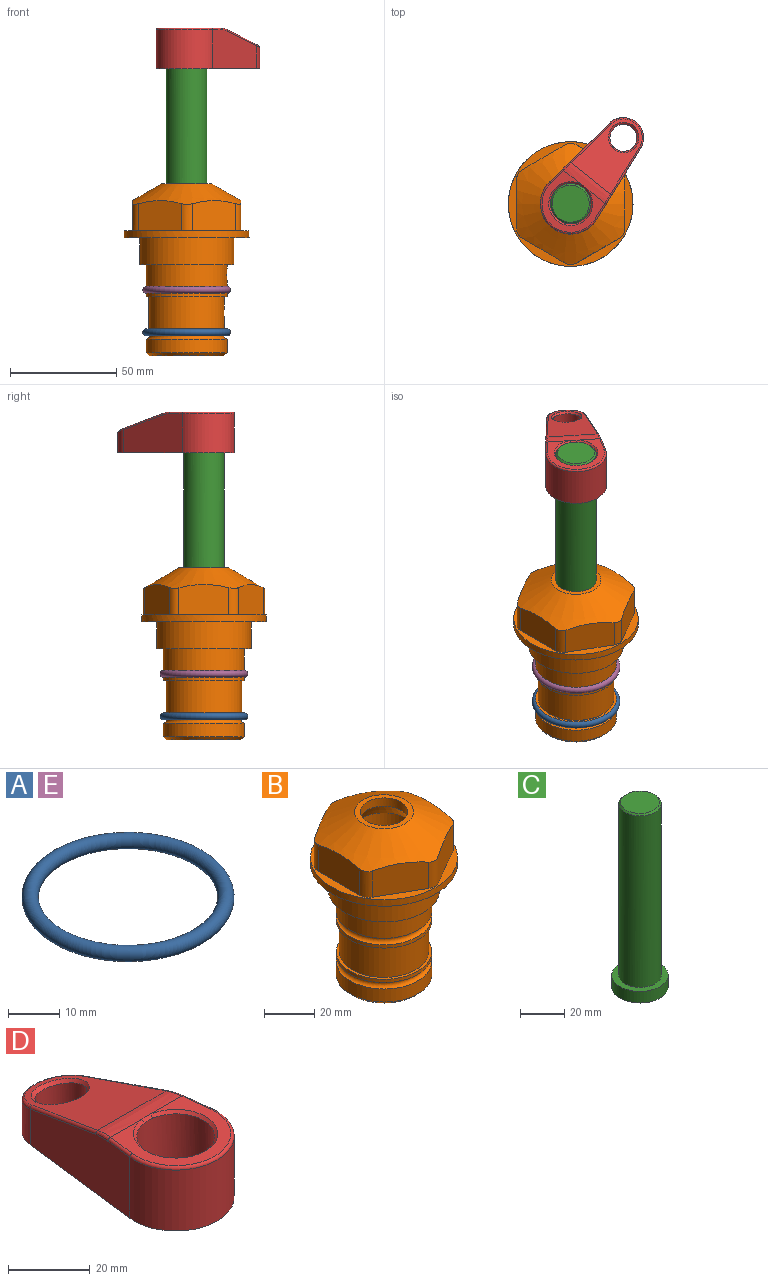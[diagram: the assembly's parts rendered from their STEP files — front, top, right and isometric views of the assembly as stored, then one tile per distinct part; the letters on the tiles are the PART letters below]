
ASSEMBLY  parts=5 mates=3
PART A: 1 faces, bbox 44.7x44.7x3.2 mm
  f0: torus R=19.05mm, axis (0,0,1), area 1193.9mm2
PART B: 36 faces, bbox 58.7x58.7x81 mm
  f0: cylinder r=17.78mm len=35.56mm, axis (0,0,1), area 1670.8mm2, adj f23,f24,f31
  f1: cylinder r=19.05mm len=38.1mm, axis (0,0,1), area 1191.9mm2, adj f26,f27,f30
  f2: plane 58.66x58.66mm, normal (0,0,-1), area 1150.6mm2, adj f3,f28
  f3: cylinder r=29.33mm len=58.66mm, axis (0,0,-1), area 585.1mm2, adj f2,f4
  f4: plane 58.66x58.66mm, normal (0,0,1), area 475.9mm2, adj f3,f5,f6,f7,f8,f9,f10,f11
  f5: plane 20.32x14.34mm, normal (-0.5,0.87,0), area 324.4mm2, adj f4,f15,f16,f17
  f6: plane 20.32x14.34mm, normal (0.5,0.87,0), area 324.4mm2, adj f4,f14,f15,f17
  f7: plane 23.48x14.34mm, normal (1,0,0), area 324.4mm2, adj f4,f13,f14,f17
  f8: plane 20.32x14.34mm, normal (0.5,-0.87,0), area 324.4mm2, adj f4,f12,f13,f17
  f9: plane 20.32x14.34mm, normal (-0.5,-0.87,0), area 324.4mm2, adj f4,f11,f12,f17
  f10: plane 23.48x14.34mm, normal (-1,0,0), area 324.4mm2, adj f4,f11,f16,f17
  f11: cylinder r=5.08mm len=12.85mm, axis (0,0,-1), area 67.2mm2, adj f4,f9,f10,f17
  f12: cylinder r=5.08mm len=12.85mm, axis (0,0,-1), area 67.2mm2, adj f4,f8,f9,f17
  f13: cylinder r=5.08mm len=12.85mm, axis (0,0,-1), area 67.2mm2, adj f4,f7,f8,f17
  f14: cylinder r=5.08mm len=12.85mm, axis (0,0,-1), area 67.2mm2, adj f4,f6,f7,f17
  f15: cylinder r=5.08mm len=12.85mm, axis (0,0,-1), area 67.2mm2, adj f4,f5,f6,f17
  f16: cylinder r=5.08mm len=12.85mm, axis (0,0,-1), area 67.2mm2, adj f4,f5,f10,f17
  f17: cone r=11.73mm half-angle=60deg, axis (0,0,-1), area 2071.8mm2, adj f5,f6,f7,f8,f9,f10,f11,f12
  f18: plane 23.46x23.46mm, normal (0,0,1), area 147.4mm2, adj f17,f35
  f19: plane 34.93x34.93mm, normal (0,0,-1), area 958mm2, adj f29
  f20: cylinder r=19.05mm len=38.1mm, axis (0,0,1), area 760.1mm2, adj f21,f29
  f21: torus R=19.05mm, axis (0,0,1), area 565.3mm2, adj f20,f22
  f22: cylinder r=19.05mm len=38.1mm, axis (0,0,1), area 190mm2, adj f21,f23
  f23: plane 38.1x38.1mm, normal (0,0,1), area 146.9mm2, adj f0,f22
  f24: plane 38.1x38.1mm, normal (0,0,-1), area 146.9mm2, adj f0,f25
  f25: cylinder r=19.05mm len=38.1mm, axis (0,0,1), area 190mm2, adj f24,f26
  f26: torus R=19.05mm, axis (0,0,1), area 565.3mm2, adj f1,f25
  f27: plane 44.45x44.45mm, normal (0,0,-1), area 411.7mm2, adj f1,f28
  f28: cylinder r=22.23mm len=44.45mm, axis (0,0,1), area 1773.5mm2, adj f2,f27
  f29: cone r=19.05mm half-angle=45deg, axis (0,0,1), area 257.5mm2, adj f19,f20
  f30: cylinder r=3.17mm len=6.75mm, axis (-1,0,0), area 128mm2, adj f1,f33
  f31: cylinder r=3.17mm len=6.35mm, axis (-1,0,0), area 102.5mm2, adj f0,f33
  f32: plane 25.4x25.4mm, normal (0,0,1), area 506.7mm2, adj f33
  f33: cylinder r=12.7mm len=66.42mm, axis (0,0,-1), area 5236.2mm2, adj f30,f31,f32,f34
  f34: cone r=9.53mm half-angle=30deg, axis (0,0,-1), area 443.4mm2, adj f33,f35
  f35: cylinder r=9.53mm len=19.05mm, axis (0,0,-1), area 240.9mm2, adj f18,f34
PART C: 6 faces, bbox 25.4x25.4x101.6 mm
  f0: plane 17.46x17.46mm, normal (0,0,1), area 239.5mm2, adj f5
  f1: plane 25.4x25.4mm, normal (0,0,-1), area 506.7mm2, adj f2
  f2: cylinder r=12.7mm len=25.4mm, axis (0,0,1), area 506.7mm2, adj f1,f3
  f3: plane 25.4x25.4mm, normal (0,0,1), area 221.7mm2, adj f2,f4
  f4: cylinder r=9.53mm len=94.46mm, axis (0,0,1), area 5653mm2, adj f3,f5
  f5: cone r=8.73mm half-angle=45deg, axis (0,0,-1), area 64.4mm2, adj f0,f4
PART D: 31 faces, bbox 31.7x65.5x19.8 mm
  f0: plane 39.12x18.26mm, normal (0.99,0.12,0), area 612.2mm2, adj f1,f4,f7,f11,f13,f15
  f1: cylinder r=9.53mm len=18.91mm, axis (0,0,-1), area 296.1mm2, adj f0,f2,f7,f17
  f2: plane 39.12x18.26mm, normal (-0.99,0.12,0), area 612.2mm2, adj f1,f4,f7,f12,f14,f16
  f3: cylinder r=6.35mm len=12.7mm, axis (0,0,-1), area 362.4mm2, adj f7,f18
  f4: cylinder r=14.29mm len=28.58mm, axis (0,0,-1), area 882.2mm2, adj f0,f2,f7,f10
  f5: cylinder r=9.53mm len=19.05mm, axis (0,0,-1), area 1092.6mm2, adj f7,f19,f20
  f6: plane 26.99x23.69mm, normal (0,0,1), area 216.2mm2, adj f9,f10,f11,f12,f19
  f7: plane 63.5x28.58mm, normal (0,0,-1), area 661.8mm2, adj f0,f1,f2,f3,f4,f5,f22,f23
  f8: plane 33.52x23.6mm, normal (0,0.26,0.97), area 486mm2, adj f9,f15,f16,f17,f18
  f9: cylinder r=19.05mm len=24.72mm, axis (1,0,0), area 120.4mm2, adj f6,f8,f13,f14,f20
  f10: torus R=13.49mm, axis (0,0,1), area 59mm2, adj f4,f6,f11,f12
  f11: cylinder r=0.79mm len=8.67mm, axis (0.12,-0.99,0), area 10.8mm2, adj f0,f6,f10,f13
  f12: cylinder r=0.79mm len=8.67mm, axis (0.12,0.99,0), area 10.8mm2, adj f2,f6,f10,f14
  f13: bspline ~4.95x1.42mm, area 6.1mm2, adj f0,f9,f11,f15
  f14: bspline ~4.95x1.42mm, area 6.1mm2, adj f2,f9,f12,f16
  f15: cylinder r=0.79mm len=25.95mm, axis (0.12,-0.96,0.26), area 32.9mm2, adj f0,f8,f13,f17
  f16: cylinder r=0.79mm len=25.95mm, axis (0.12,0.96,-0.26), area 32.9mm2, adj f2,f8,f14,f17
  f17: bspline ~18.91x8.38mm, area 30mm2, adj f1,f8,f15,f16
  f18: bspline ~14.29x14.29mm, area 48.3mm2, adj f3,f8
  f19: cone r=9.53mm half-angle=45deg, axis (0,0,1), area 66.5mm2, adj f5,f6,f20
  f20: bspline ~3.22x0.96mm, area 3.5mm2, adj f5,f9,f19
  f21: plane 2.75x2.72mm, normal (0,0,-1), area 2.9mm2, adj f23,f25,f28
  f22: plane 23.05x15.88mm, normal (-0.99,-0.12,0), area 323.6mm2, adj f7,f25,f26,f27,f28,f29
  f23: plane 23.05x15.88mm, normal (0.99,-0.12,0), area 323.6mm2, adj f7,f21,f25,f27,f28,f30
  f24: cylinder r=9.53mm len=10.69mm, axis (0,0,-1), area 114.7mm2, adj f7,f27,f29,f30
  f25: cylinder r=12.7mm len=20.59mm, axis (0,0,-1), area 381.1mm2, adj f7,f21,f22,f23,f26,f28
  f26: plane 2.75x2.72mm, normal (0,0,-1), area 2.9mm2, adj f22,f25,f28
  f27: plane 19.72x18.37mm, normal (0,-0.26,-0.97), area 291.8mm2, adj f22,f23,f24,f28,f29,f30
  f28: cylinder r=15.88mm len=19.92mm, axis (1,0,0), area 54.8mm2, adj f21,f22,f23,f25,f26,f27
  f29: cylinder r=1.59mm len=11mm, axis (0,0,-1), area 34.7mm2, adj f7,f22,f24,f27
  f30: cylinder r=1.59mm len=11mm, axis (0,0,-1), area 34.7mm2, adj f7,f23,f24,f27
PART E: same geometry as A
PLACE A t=(0,0,-20)mm
PLACE B at identity fixed
PLACE C rot(axis=(0,0,-1),38.7deg) t=(0,0,35.17)mm
PLACE D rot(axis=(0,0,-1),38.7deg) t=(0,0,35.17)mm
PLACE E at identity
MATE fastened C.f2 <-> D.f4  axis (0,0,1) through (0,0,97.88)mm
MATE fastened A.f0 <-> B.f0  axis (0,0,1) through (0,0,-44.51)mm
MATE cylindrical C.f2 <-> B.f0  axis (0,0,-1) through (0,0,-2.93)mm
